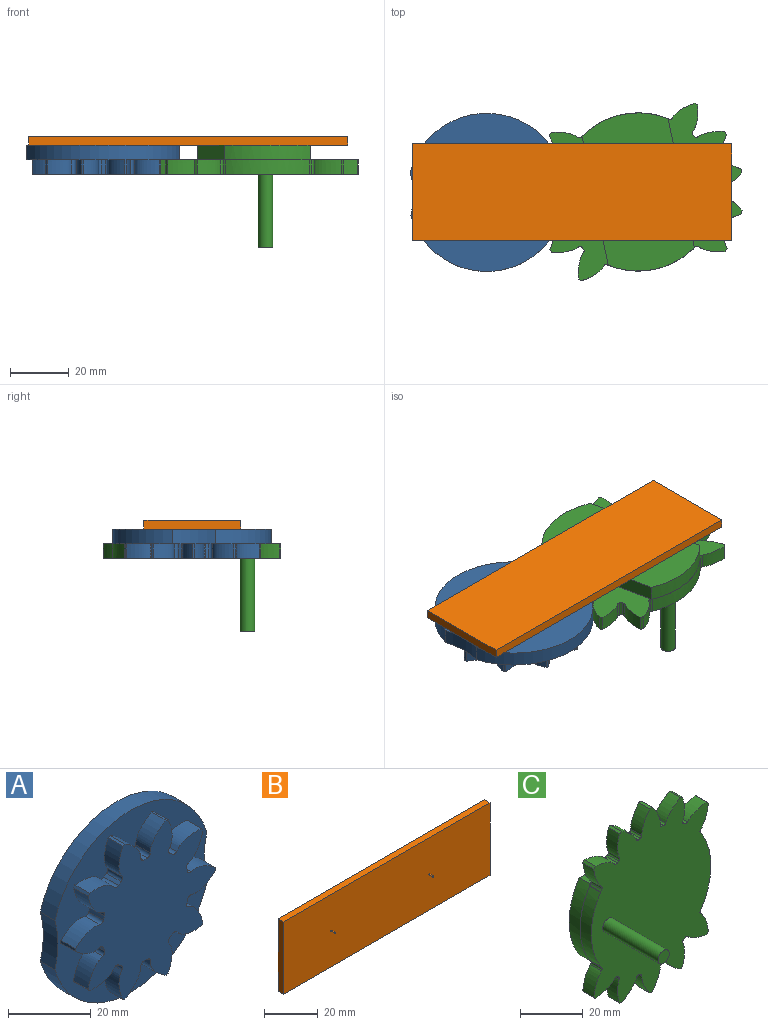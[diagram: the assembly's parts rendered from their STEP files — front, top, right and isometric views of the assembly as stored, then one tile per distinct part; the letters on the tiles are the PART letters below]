
ASSEMBLY  parts=3 mates=2
PART A: 67 faces, bbox 52x10x54 mm
  f0: plane 54x52mm, normal (0,-1,0), area 1038.6mm2, adj f1,f2,f4,f5,f6,f7,f8,f9
  f1: cylinder r=27mm len=52mm, axis (0,-1,0), area 350.4mm2, adj f0,f3,f65,f66
  f2: cylinder r=27mm len=52mm, axis (0,-1,0), area 350.4mm2, adj f0,f3,f65,f66
  f3: plane 54x52mm, normal (0,1,0), area 2251.2mm2, adj f1,f2,f65,f66
  f4: extruded ~7.03x5.4mm, area 46.2mm2, adj f0,f43,f44,f45
  f5: cylinder r=15mm len=5mm, axis (0,1,0), area 5.8mm2, adj f0,f44,f45,f46
  f6: extruded ~7.03x5.4mm, area 46.2mm2, adj f0,f7,f44,f46
  f7: cylinder r=24mm len=5mm, axis (0,1,0), area 3.9mm2, adj f0,f6,f8,f44
  f8: extruded ~8.86x5mm, area 46.2mm2, adj f0,f7,f44,f47
  f9: cylinder r=15mm len=5mm, axis (0,1,0), area 5.8mm2, adj f0,f44,f47,f48
  f10: extruded ~8.5x5mm, area 46.2mm2, adj f0,f11,f44,f48
  f11: cylinder r=24mm len=5mm, axis (0,1,0), area 3.9mm2, adj f0,f10,f12,f44
  f12: extruded ~7.31x5.02mm, area 46.2mm2, adj f0,f11,f44,f49
  f13: cylinder r=15mm len=5mm, axis (0,1,0), area 5.8mm2, adj f0,f44,f49,f50
  f14: extruded ~8.35x5mm, area 46.2mm2, adj f0,f15,f44,f50
  f15: cylinder r=24mm len=5mm, axis (0,1,0), area 3.9mm2, adj f0,f14,f16,f44
  f16: extruded ~8.35x5mm, area 46.2mm2, adj f0,f15,f44,f51
  f17: cylinder r=15mm len=5mm, axis (0,1,0), area 5.8mm2, adj f0,f44,f51,f52
  f18: extruded ~7.31x5.02mm, area 46.2mm2, adj f0,f19,f44,f52
  f19: cylinder r=24mm len=5mm, axis (0,1,0), area 3.9mm2, adj f0,f18,f20,f44
  f20: extruded ~8.5x5mm, area 46.2mm2, adj f0,f19,f44,f53
  f21: cylinder r=15mm len=5mm, axis (0,1,0), area 5.8mm2, adj f0,f44,f53,f54
  f22: extruded ~8.86x5mm, area 46.2mm2, adj f0,f23,f44,f54
  f23: cylinder r=24mm len=5mm, axis (0,1,0), area 3.9mm2, adj f0,f22,f24,f44
  f24: extruded ~7.03x5.4mm, area 46.2mm2, adj f0,f23,f44,f55
  f25: cylinder r=15mm len=5mm, axis (0,1,0), area 5.8mm2, adj f0,f44,f55,f56
  f26: extruded ~7.03x5.4mm, area 46.2mm2, adj f0,f27,f44,f56
  f27: cylinder r=24mm len=5mm, axis (0,1,0), area 3.9mm2, adj f0,f26,f28,f44
  f28: extruded ~8.86x5mm, area 46.2mm2, adj f0,f27,f44,f57
  f29: cylinder r=15mm len=5mm, axis (0,1,0), area 5.8mm2, adj f0,f44,f57,f58
  f30: extruded ~8.5x5mm, area 46.2mm2, adj f0,f31,f44,f58
  f31: cylinder r=24mm len=5mm, axis (0,1,0), area 3.9mm2, adj f0,f30,f32,f44
  f32: extruded ~7.31x5.02mm, area 46.2mm2, adj f0,f31,f44,f59
  f33: cylinder r=15mm len=5mm, axis (0,1,0), area 5.8mm2, adj f0,f44,f59,f60
  f34: extruded ~8.35x5mm, area 46.2mm2, adj f0,f35,f44,f60
  f35: cylinder r=24mm len=5mm, axis (0,1,0), area 3.9mm2, adj f0,f34,f36,f44
  f36: extruded ~8.35x5mm, area 46.2mm2, adj f0,f35,f44,f61
  f37: cylinder r=15mm len=5mm, axis (0,1,0), area 5.8mm2, adj f0,f44,f61,f62
  f38: extruded ~7.31x5.02mm, area 46.2mm2, adj f0,f39,f44,f62
  f39: cylinder r=24mm len=5mm, axis (0,1,0), area 3.9mm2, adj f0,f38,f40,f44
  f40: extruded ~8.5x5mm, area 46.2mm2, adj f0,f39,f44,f63
  f41: cylinder r=15mm len=5mm, axis (0,1,0), area 5.8mm2, adj f0,f44,f63,f64
  f42: extruded ~8.86x5mm, area 46.2mm2, adj f0,f43,f44,f64
  f43: cylinder r=24mm len=5mm, axis (0,1,0), area 3.9mm2, adj f0,f4,f42,f44
  f44: plane 48.08x45.97mm, normal (0,-1,0), area 1212.6mm2, adj f4,f5,f6,f7,f8,f9,f10,f11
  f45: cylinder r=1.03mm len=5mm, axis (0,1,0), area 7.8mm2, adj f0,f4,f5,f44
  f46: cylinder r=1.03mm len=5mm, axis (0,1,0), area 7.8mm2, adj f0,f5,f6,f44
  f47: cylinder r=1.03mm len=5mm, axis (0,1,0), area 7.8mm2, adj f0,f8,f9,f44
  f48: cylinder r=1.03mm len=5mm, axis (0,1,0), area 7.8mm2, adj f0,f9,f10,f44
  f49: cylinder r=1.03mm len=5mm, axis (0,1,0), area 7.8mm2, adj f0,f12,f13,f44
  f50: cylinder r=1.03mm len=5mm, axis (0,1,0), area 7.8mm2, adj f0,f13,f14,f44
  f51: cylinder r=1.03mm len=5mm, axis (0,1,0), area 7.8mm2, adj f0,f16,f17,f44
  f52: cylinder r=1.03mm len=5mm, axis (0,1,0), area 7.8mm2, adj f0,f17,f18,f44
  f53: cylinder r=1.03mm len=5mm, axis (0,1,0), area 7.8mm2, adj f0,f20,f21,f44
  f54: cylinder r=1.03mm len=5mm, axis (0,1,0), area 7.8mm2, adj f0,f21,f22,f44
  f55: cylinder r=1.03mm len=5mm, axis (0,1,0), area 7.8mm2, adj f0,f24,f25,f44
  f56: cylinder r=1.03mm len=5mm, axis (0,1,0), area 7.8mm2, adj f0,f25,f26,f44
  f57: cylinder r=1.03mm len=5mm, axis (0,1,0), area 7.8mm2, adj f0,f28,f29,f44
  f58: cylinder r=1.03mm len=5mm, axis (0,1,0), area 7.8mm2, adj f0,f29,f30,f44
  f59: cylinder r=1.03mm len=5mm, axis (0,1,0), area 7.8mm2, adj f0,f32,f33,f44
  f60: cylinder r=1.03mm len=5mm, axis (0,1,0), area 7.8mm2, adj f0,f33,f34,f44
  f61: cylinder r=1.03mm len=5mm, axis (0,1,0), area 7.8mm2, adj f0,f36,f37,f44
  f62: cylinder r=1.03mm len=5mm, axis (0,1,0), area 7.8mm2, adj f0,f37,f38,f44
  f63: cylinder r=1.03mm len=5mm, axis (0,1,0), area 7.8mm2, adj f0,f40,f41,f44
  f64: cylinder r=1.03mm len=5mm, axis (0,1,0), area 7.8mm2, adj f0,f41,f42,f44
  f65: cylinder r=27mm len=14.56mm, axis (0,1,0), area 73.7mm2, adj f0,f1,f2,f3
  f66: cylinder r=27mm len=14.56mm, axis (0,1,0), area 73.7mm2, adj f0,f1,f2,f3
PART B: 10 faces, bbox 108.9x5x33.1 mm
  f0: plane 33.08x3mm, normal (-1,0,0), area 99.3mm2, adj f1,f3,f4,f5
  f1: plane 108.91x3mm, normal (0,0,-1), area 326.7mm2, adj f0,f2,f4,f5
  f2: plane 33.08x3mm, normal (1,0,0), area 99.3mm2, adj f1,f3,f4,f5
  f3: plane 108.91x3mm, normal (0,0,1), area 326.7mm2, adj f0,f2,f4,f5
  f4: plane 108.91x33.08mm, normal (0,-1,0), area 3602.8mm2, adj f0,f1,f2,f3,f6,f8
  f5: plane 108.91x33.08mm, normal (0,1,0), area 3603.2mm2, adj f0,f1,f2,f3
  f6: cylinder r=0.25mm len=2mm, axis (0,1,0), area 3.1mm2, adj f4,f7
  f7: plane 0.5x0.5mm, normal (0,-1,0), area 0.2mm2, adj f6
  f8: cylinder r=0.25mm len=2mm, axis (0,1,0), area 3.1mm2, adj f4,f9
  f9: plane 0.5x0.5mm, normal (0,-1,0), area 0.2mm2, adj f8
PART C: 81 faces, bbox 54x35x72 mm
  f0: plane 51.67x21mm, normal (0,1,0), area 653.6mm2, adj f40,f41,f42,f43,f44,f45,f46,f47
  f1: plane 29.65x4.55mm, normal (0,1,0), area 0mm2, adj f4,f39,f72,f75
  f2: plane 29.29x4.32mm, normal (0,1,0), area 0mm2, adj f3,f6,f38,f71,f73,f77
  f3: plane 5x0.03mm, normal (-0.48,0,-0.88), area 0.2mm2, adj f2,f6,f27,f73
  f4: cylinder r=27mm len=29.94mm, axis (0,1,0), area 158.7mm2, adj f1,f5,f27,f33,f39
  f5: plane 51.67x21mm, normal (0,1,0), area 653.6mm2, adj f4,f7,f8,f9,f10,f11,f12,f13
  f6: cylinder r=0.8mm len=5mm, axis (0,1,0), area 1.2mm2, adj f2,f3,f16,f27
  f7: extruded ~8.56x5mm, area 47.4mm2, adj f5,f26,f27,f28
  f8: cylinder r=27mm len=5mm, axis (0,1,0), area 4.3mm2, adj f5,f27,f28,f29
  f9: extruded ~6.66x6.51mm, area 47.4mm2, adj f5,f10,f27,f29
  f10: cylinder r=36mm len=5mm, axis (0,1,0), area 5.4mm2, adj f5,f9,f11,f27
  f11: extruded ~9.31x5mm, area 47.4mm2, adj f5,f10,f27,f30
  f12: cylinder r=27mm len=5mm, axis (0,1,0), area 4.3mm2, adj f5,f27,f30,f31
  f13: extruded ~8.64x5mm, area 47.4mm2, adj f5,f14,f27,f31
  f14: cylinder r=36mm len=5mm, axis (0,1,0), area 5.4mm2, adj f5,f13,f15,f27
  f15: extruded ~8.64x5mm, area 47.4mm2, adj f5,f14,f27,f32
  f16: cylinder r=27mm len=5mm, axis (0,1,0), area 4.3mm2, adj f5,f6,f27,f32,f77
  f17: extruded ~8.64x5mm, area 47.4mm2, adj f5,f18,f27,f33
  f18: cylinder r=36mm len=5mm, axis (0,1,0), area 5.4mm2, adj f5,f17,f19,f27
  f19: extruded ~8.64x5mm, area 47.4mm2, adj f5,f18,f27,f34
  f20: cylinder r=27mm len=5mm, axis (0,1,0), area 4.3mm2, adj f5,f27,f34,f35
  f21: extruded ~9.31x5mm, area 47.4mm2, adj f5,f22,f27,f35
  f22: cylinder r=36mm len=5mm, axis (0,1,0), area 5.4mm2, adj f5,f21,f23,f27
  f23: extruded ~6.66x6.51mm, area 47.4mm2, adj f5,f22,f27,f36
  f24: cylinder r=27mm len=5mm, axis (0,1,0), area 4.3mm2, adj f5,f27,f36,f37
  f25: extruded ~8.56x5mm, area 47.4mm2, adj f5,f26,f27,f37
  f26: cylinder r=36mm len=5mm, axis (0,1,0), area 5.4mm2, adj f5,f7,f25,f27
  f27: plane 72x54mm, normal (0,-1,0), area 2819.8mm2, adj f3,f4,f6,f7,f8,f9,f10,f11
  f28: cylinder r=0.8mm len=5mm, axis (0,1,0), area 6mm2, adj f5,f7,f8,f27
  f29: cylinder r=0.8mm len=5mm, axis (0,1,0), area 6mm2, adj f5,f8,f9,f27
  f30: cylinder r=0.8mm len=5mm, axis (0,1,0), area 6mm2, adj f5,f11,f12,f27
  f31: cylinder r=0.8mm len=5mm, axis (0,1,0), area 6mm2, adj f5,f12,f13,f27
  f32: cylinder r=0.8mm len=5mm, axis (0,1,0), area 6mm2, adj f5,f15,f16,f27
  f33: cylinder r=0.8mm len=5mm, axis (0,1,0), area 6mm2, adj f4,f5,f17,f27
  f34: cylinder r=0.8mm len=5mm, axis (0,1,0), area 6mm2, adj f5,f19,f20,f27
  f35: cylinder r=0.8mm len=5mm, axis (0,1,0), area 6mm2, adj f5,f20,f21,f27
  f36: cylinder r=0.8mm len=5mm, axis (0,1,0), area 6mm2, adj f5,f23,f24,f27
  f37: cylinder r=0.8mm len=5mm, axis (0,1,0), area 6mm2, adj f5,f24,f25,f27
  f38: plane 5x0mm, normal (-0.48,0,0.88), area 0mm2, adj f2,f27,f71,f73
  f39: plane 5x0mm, normal (0.39,0,0.92), area 0mm2, adj f1,f4,f27,f72
  f40: cylinder r=0.8mm len=5mm, axis (0,1,0), area 6mm2, adj f0,f27,f41,f69
  f41: extruded ~8.64x5mm, area 47.4mm2, adj f0,f27,f40,f42
  f42: cylinder r=36mm len=5mm, axis (0,1,0), area 5.4mm2, adj f0,f27,f41,f43
  f43: extruded ~8.64x5mm, area 47.4mm2, adj f0,f27,f42,f44
  f44: cylinder r=0.8mm len=5mm, axis (0,1,0), area 6mm2, adj f0,f27,f43,f45
  f45: cylinder r=27mm len=5mm, axis (0,1,0), area 4.3mm2, adj f0,f27,f44,f46
  f46: cylinder r=0.8mm len=5mm, axis (0,1,0), area 6mm2, adj f0,f27,f45,f47
  f47: extruded ~9.31x5mm, area 47.4mm2, adj f0,f27,f46,f48
  f48: cylinder r=36mm len=5mm, axis (0,1,0), area 5.4mm2, adj f0,f27,f47,f49
  f49: extruded ~6.66x6.51mm, area 47.4mm2, adj f0,f27,f48,f50
  f50: cylinder r=0.8mm len=5mm, axis (0,1,0), area 6mm2, adj f0,f27,f49,f51
  f51: cylinder r=27mm len=5mm, axis (0,1,0), area 4.3mm2, adj f0,f27,f50,f52
  f52: cylinder r=0.8mm len=5mm, axis (0,1,0), area 6mm2, adj f0,f27,f51,f53
  f53: extruded ~8.56x5mm, area 47.4mm2, adj f0,f27,f52,f54
  f54: cylinder r=36mm len=5mm, axis (0,1,0), area 5.4mm2, adj f0,f27,f53,f55
  f55: extruded ~8.56x5mm, area 47.4mm2, adj f0,f27,f54,f56
  f56: cylinder r=0.8mm len=5mm, axis (0,1,0), area 6mm2, adj f0,f27,f55,f57
  f57: cylinder r=27mm len=5mm, axis (0,1,0), area 4.3mm2, adj f0,f27,f56,f58
  f58: cylinder r=0.8mm len=5mm, axis (0,1,0), area 6mm2, adj f0,f27,f57,f59
  f59: extruded ~6.66x6.51mm, area 47.4mm2, adj f0,f27,f58,f60
  f60: cylinder r=36mm len=5mm, axis (0,1,0), area 5.4mm2, adj f0,f27,f59,f61
  f61: extruded ~9.31x5mm, area 47.4mm2, adj f0,f27,f60,f62
  f62: cylinder r=0.8mm len=5mm, axis (0,1,0), area 6mm2, adj f0,f27,f61,f63
  f63: cylinder r=27mm len=5mm, axis (0,1,0), area 4.3mm2, adj f0,f27,f62,f64
  f64: cylinder r=0.8mm len=5mm, axis (0,1,0), area 6mm2, adj f0,f27,f63,f65
  f65: extruded ~8.64x5mm, area 47.4mm2, adj f0,f27,f64,f66
  f66: cylinder r=36mm len=5mm, axis (0,1,0), area 5.4mm2, adj f0,f27,f65,f67
  f67: extruded ~8.64x5mm, area 47.4mm2, adj f0,f27,f66,f68
  f68: cylinder r=0.8mm len=5mm, axis (0,1,0), area 6mm2, adj f0,f27,f67,f70
  f69: cylinder r=27mm len=5mm, axis (0,1,0), area 4.3mm2, adj f0,f27,f40,f71,f77
  f70: cylinder r=27mm len=5mm, axis (0,1,0), area 4.3mm2, adj f0,f27,f68,f72,f75
  f71: cylinder r=0.8mm len=5mm, axis (0,1,0), area 0.4mm2, adj f2,f27,f38,f69
  f72: cylinder r=0.8mm len=5mm, axis (0,1,0), area 0.3mm2, adj f1,f27,f39,f70
  f73: cylinder r=27mm len=29.04mm, axis (0,1,0), area 153.3mm2, adj f2,f3,f27,f38
  f74: plane 44.9x5mm, normal (0,0,-1), area 224.5mm2, adj f0,f75,f77,f78
  f75: cylinder r=27.01mm len=30mm, axis (0,1,0), area 159mm2, adj f1,f70,f74,f76,f78
  f76: plane 44.9x5mm, normal (0,0,1), area 224.5mm2, adj f5,f75,f77,f78
  f77: cylinder r=27.01mm len=30mm, axis (0,1,0), area 159mm2, adj f2,f16,f69,f74,f76,f78
  f78: plane 54x30mm, normal (0,1,0), area 1532.2mm2, adj f74,f75,f76,f77
  f79: cylinder r=2.5mm len=25mm, axis (0,1,0), area 392.7mm2, adj f27,f80
  f80: plane 5x5mm, normal (0,-1,0), area 19.6mm2, adj f79
PLACE A rot(axis=(1,0.01,0.01),90deg) t=(-83.74,-0.01,-3)mm
PLACE B rot(axis=(1,0,0),90deg) t=(-59.24,16.54,0)mm
PLACE C rot(axis=(0.5,0.61,0.61),126.9deg) t=(-31.99,0.15,-3)mm
MATE revolute B.f6 <-> A.f1  axis (0,0,-1) through (-83.74,-0.01,-3)mm
MATE revolute B.f8 <-> C.f77  axis (0,0,-1) through (-31.99,0.16,-3)mm
